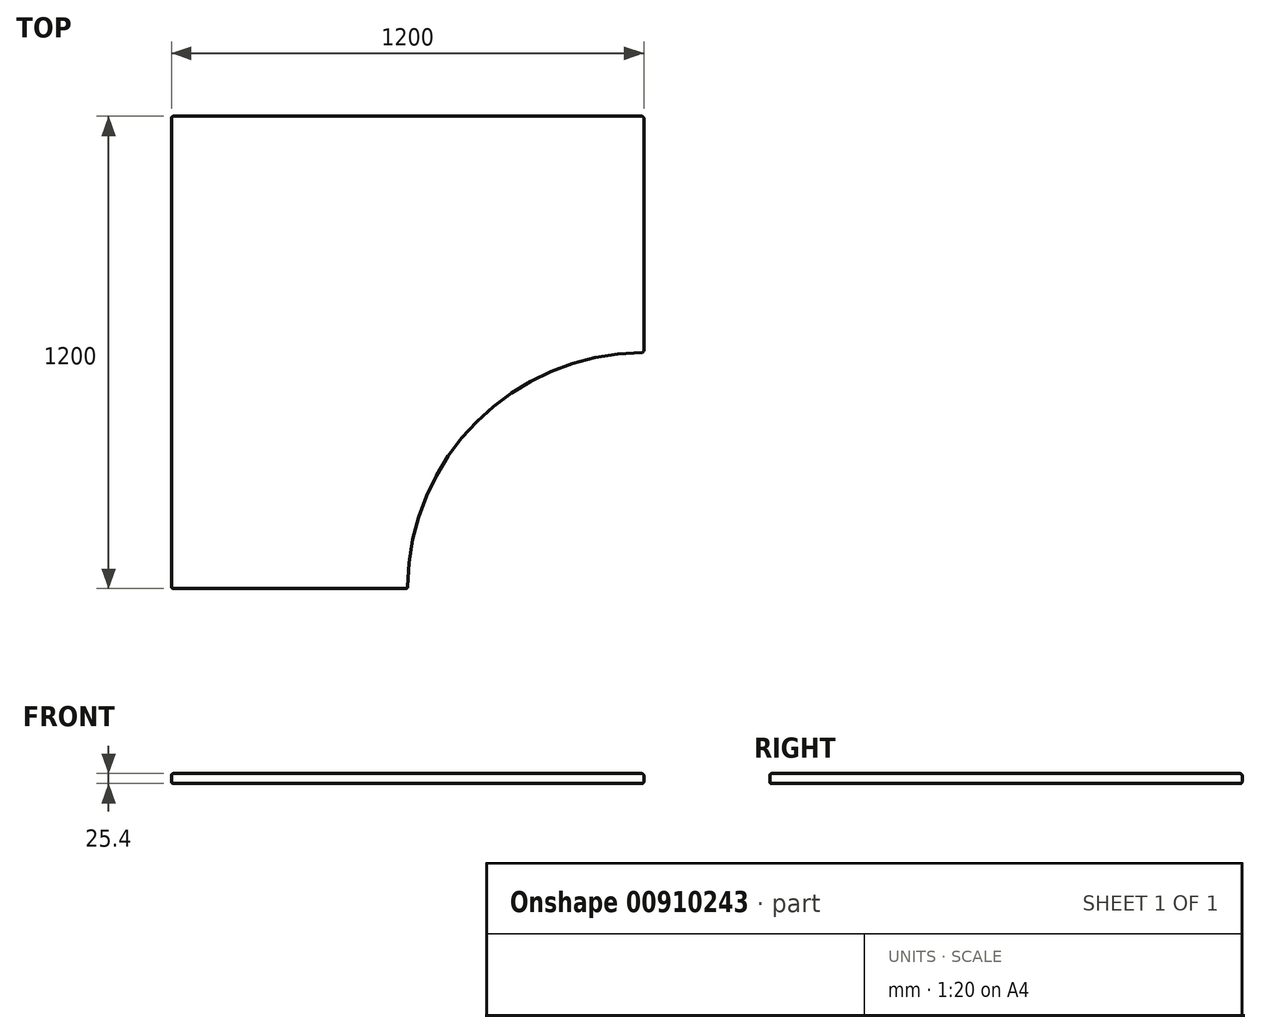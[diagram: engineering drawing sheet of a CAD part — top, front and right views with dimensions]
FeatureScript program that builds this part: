
annotation { "Feature Type Name" : "Feature", "Feature Type Description" : "" }
export const myFeature = defineFeature(function(context is Context, id is Id, definition is map)
    precondition{}
    {
        {
            var Q0;
            Q0=qCreatedBy(makeId("Top.planeOp"),FACE);
            var sketch = newSketch(context, id + "F0", { "sketchPlane" : qUnion([Q0])});
            skLineSegment(sketch, "E0.bottom", {"start": v(596.82, 724.99) * mm, "end": v(-603.18, 724.99) * mm});
            skLineSegment(sketch, "E0.top", {"start": v(-3.18, -475) * mm, "end": v(-603.18, -475) * mm});
            skLineSegment(sketch, "E0.left", {"start": v(596.82, 724.99) * mm, "end": v(596.82, 124.99) * mm});
            skLineSegment(sketch, "E0.right", {"start": v(-603.18, 724.99) * mm, "end": v(-603.18, -475) * mm});
            skArc(sketch, "E1", {"start": v(596.82, 124.99) * mm, "mid": v(172.55, -50.75) * mm, "end": v(-3.18, -475) * mm});
            skSolve(sketch);
        }
        {
            var Q0;
            Q0=makeQuery(id+"F0.imprint","IMPRINT",FACE,{"disambiguationData":[TD([[makeQuery(id+"F0.imprint","IMPRINT",EDGE,{"derivedFrom":sQuery(id+"F0.wireOp",EDGE,"E0.bottom")}),1.0]])]});
            extrude(context, id + "F1", {"entities" : qUnion([Q0]), "depth" : 25.4 * mm, "offsetDistance" : 25.4 * mm});
        }
        {
            var Q0;
            Q0=makeQuery(id+"F1.opExtrude","SWEPT_EDGE",EDGE,{"disambiguationData":[OSD([sQuery(id+"F0.wireOp",EDGE,"E0.top"),sQuery(id+"F0.wireOp",EDGE,"E0.right")])]});
            fillet(context, id + "F2", {"entities" : qUnion([Q0]), "radius" : 5.08 * mm, "tangentPropagation" : true, "allowEdgeOverflow" : false});
        }
        {
            var Q0;
            Q0=makeQuery(id+"F1.opExtrude","SWEPT_EDGE",EDGE,{"disambiguationData":[OSD([sQuery(id+"F0.wireOp",EDGE,"E0.top"),sQuery(id+"F0.wireOp",EDGE,"E1")])]});
            fillet(context, id + "F3", {"entities" : qUnion([Q0]), "radius" : 5.08 * mm, "tangentPropagation" : true, "allowEdgeOverflow" : false});
        }
        {
            var Q0;
            Q0=makeQuery(id+"F1.opExtrude","SWEPT_EDGE",EDGE,{"disambiguationData":[OSD([sQuery(id+"F0.wireOp",EDGE,"E0.left"),sQuery(id+"F0.wireOp",EDGE,"E1")])]});
            fillet(context, id + "F4", {"entities" : qUnion([Q0]), "radius" : 5.08 * mm, "tangentPropagation" : true, "allowEdgeOverflow" : false});
        }
        {
            var Q0;
            Q0=makeQuery(id+"F1.opExtrude","SWEPT_EDGE",EDGE,{"disambiguationData":[OSD([sQuery(id+"F0.wireOp",EDGE,"E0.bottom"),sQuery(id+"F0.wireOp",EDGE,"E0.left")])]});
            fillet(context, id + "F5", {"entities" : qUnion([Q0]), "radius" : 5.08 * mm, "tangentPropagation" : true, "allowEdgeOverflow" : false});
        }
        {
            var Q0;
            Q0=makeQuery(id+"F1.opExtrude","SWEPT_EDGE",EDGE,{"disambiguationData":[OSD([sQuery(id+"F0.wireOp",EDGE,"E0.bottom"),sQuery(id+"F0.wireOp",EDGE,"E0.right")])]});
            fillet(context, id + "F6", {"entities" : qUnion([Q0]), "radius" : 5.08 * mm, "tangentPropagation" : true, "allowEdgeOverflow" : false});
        }
        {
            var Q0;
            Q0=makeQuery(id+"F1.opExtrude","CAP_FACE",FACE,{"disambiguationData":[OSD([sQuery(id+"F0.wireOp",EDGE,"E0.bottom"),sQuery(id+"F0.wireOp",EDGE,"E0.top"),sQuery(id+"F0.wireOp",EDGE,"E0.left"),sQuery(id+"F0.wireOp",EDGE,"E0.right"),sQuery(id+"F0.wireOp",EDGE,"E1")])],"isStart":true});
            var sketch = newSketch(context, id + "F7", { "sketchPlane" : qUnion([Q0])});
            skLineSegment(sketch, "E2.bottom", {"start": v(-552.38, -674.19) * mm, "end": v(546.02, -674.19) * mm, "construction": true});
            skLineSegment(sketch, "E2.top", {"start": v(-552.38, 424.2) * mm, "end": v(546.02, 424.2) * mm, "construction": true});
            skLineSegment(sketch, "E2.left", {"start": v(-552.38, -674.19) * mm, "end": v(-552.38, 424.2) * mm, "construction": true});
            skLineSegment(sketch, "E2.right", {"start": v(546.02, -674.19) * mm, "end": v(546.02, 424.2) * mm, "construction": true});
            skCircle(sketch, "E3", {"center": v(-552.38, 424.2) * mm, "radius": 22.23 * mm});
            skCircle(sketch, "E4", {"center": v(-552.38, -674.19) * mm, "radius": 22.23 * mm});
            skCircle(sketch, "E5", {"center": v(-52, 424.2) * mm, "radius": 22.23 * mm});
            skCircle(sketch, "E6", {"center": v(546.02, -173.8) * mm, "radius": 22.23 * mm});
            skCircle(sketch, "E7", {"center": v(546.02, -674.19) * mm, "radius": 22.23 * mm});
            skSolve(sketch);
        }
        {
            var Q0;
            Q0=sQuery(id+"F7.wireOp",EDGE,"E2.top");
            var Q1;
            Q1=sQuery(id+"F7.wireOp",EDGE,"E2.right");
            var Q2;
            Q2=sQuery(id+"F7.wireOp",EDGE,"E2.bottom");
            var Q3;
            Q3=sQuery(id+"F7.wireOp",EDGE,"E2.left");
            var Q4;
            Q4=sQuery(id+"F7.wireOp",EDGE,"E3");
            var Q5;
            Q5=sQuery(id+"F7.wireOp",EDGE,"E5");
            var Q6;
            Q6=sQuery(id+"F7.wireOp",EDGE,"E4");
            var Q7;
            Q7=sQuery(id+"F7.wireOp",EDGE,"E7");
            var Q8;
            Q8=sQuery(id+"F7.wireOp",EDGE,"E6");
            extrude(context, id + "F8", {"bodyType" : ToolBodyType.SURFACE, "surfaceEntities" : qUnion([Q0, Q1, Q2, Q3, Q4, Q5, Q6, Q7, Q8]), "depth" : 881.38 * mm, "offsetDistance" : 25.4 * mm});
        }
        {
            var Q0;
            Q0=makeQuery(id+"F1.opExtrude","CAP_EDGE",EDGE,{"disambiguationData":[OSD([sQuery(id+"F0.wireOp",EDGE,"E0.top")])],"isStart":true});
            fillet(context, id + "F9", {"entities" : qUnion([Q0]), "radius" : 5.08 * mm, "tangentPropagation" : true, "allowEdgeOverflow" : false});
        }
        {
            var Q0;
            Q0=makeQuery(id+"F1.opExtrude","CAP_EDGE",EDGE,{"disambiguationData":[OSD([sQuery(id+"F0.wireOp",EDGE,"E0.top")])],"isStart":false});
            fillet(context, id + "F10", {"entities" : qUnion([Q0]), "radius" : 5.08 * mm, "tangentPropagation" : true, "allowEdgeOverflow" : false});
        }
    });
